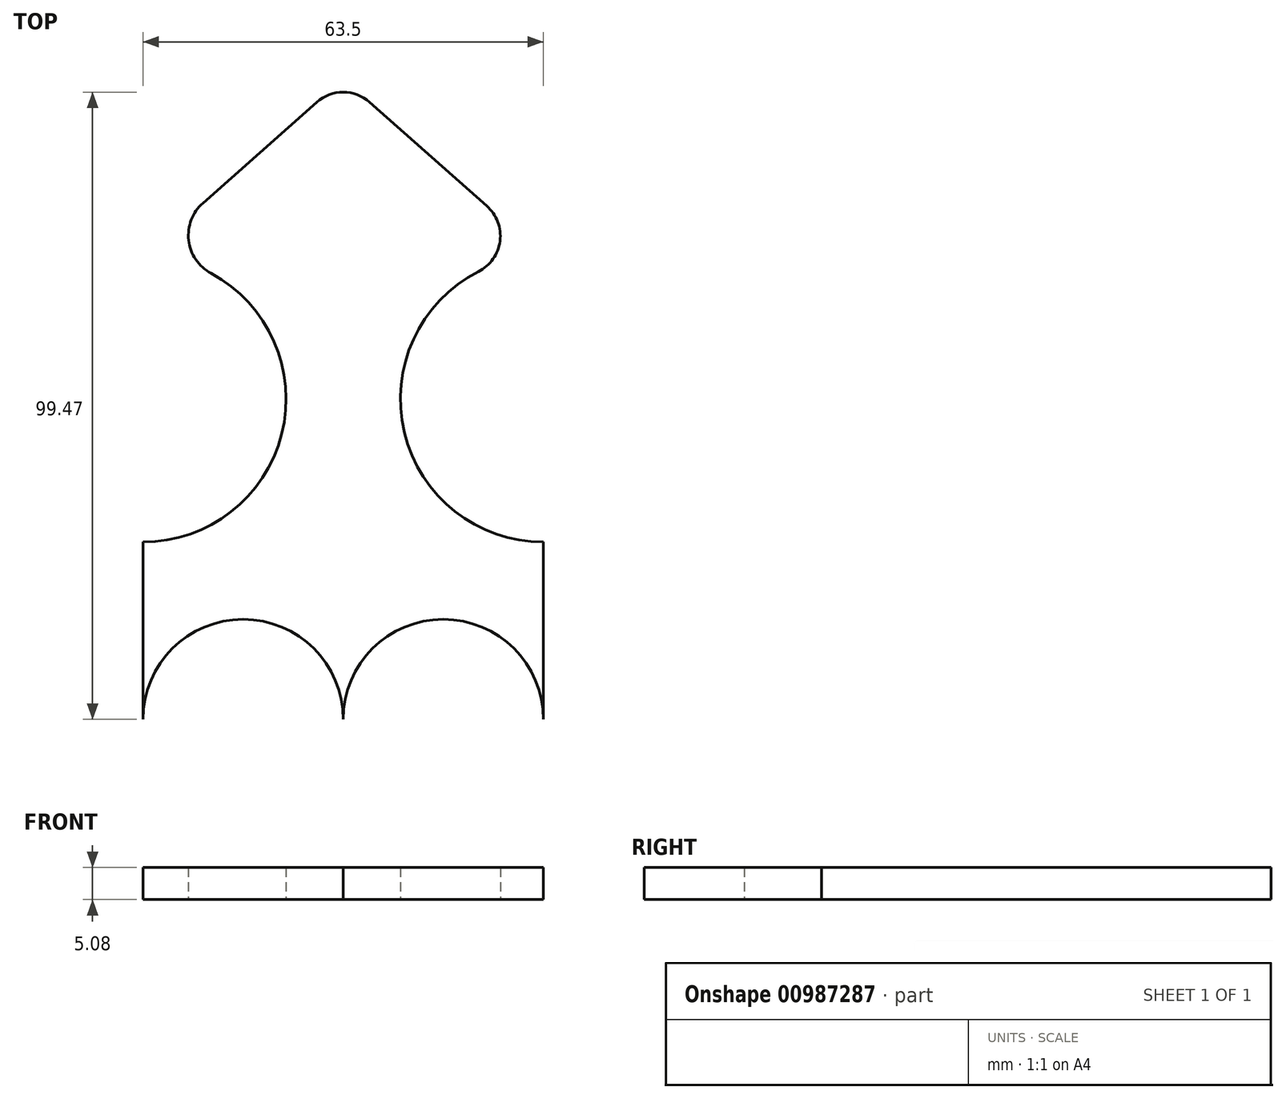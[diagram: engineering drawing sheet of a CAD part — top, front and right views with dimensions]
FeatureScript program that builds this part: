
annotation { "Feature Type Name" : "Feature", "Feature Type Description" : "" }
export const myFeature = defineFeature(function(context is Context, id is Id, definition is map)
    precondition{}
    {
        {
            var Q0;
            Q0=qCreatedBy(makeId("Top.planeOp"),FACE);
            var sketch = newSketch(context, id + "F0", { "sketchPlane" : qUnion([Q0])});
            skLineSegment(sketch, "E0", {"start": v(-31.75, 0) * mm, "end": v(-31.75, -101.6) * mm, "construction": true});
            skLineSegment(sketch, "E1", {"start": v(0, -50.8) * mm, "end": v(-63.5, -50.8) * mm, "construction": true});
            skArc(sketch, "E2", {"start": v(-63.5, -73.48) * mm, "mid": v(-41.5, -56.36) * mm, "end": v(-52.72, -30.84) * mm});
            skArc(sketch, "E3.1.0.0", {"start": v(-10.3, -30.59) * mm, "mid": v(-22.06, -56.1) * mm, "end": v(0, -73.48) * mm});
            skLineSegment(sketch, "E3.direction1", {"start": v(-63.5, -50.8) * mm, "end": v(0, -50.8) * mm, "construction": true});
            skLineSegment(sketch, "E4.trimOffspring", {"start": v(-63.5, -73.48) * mm, "end": v(-63.5, -101.6) * mm});
            skLineSegment(sketch, "E5.trimOffspring", {"start": v(0, -73.48) * mm, "end": v(0, -101.6) * mm});
            skArc(sketch, "E6", {"start": v(-31.75, -101.6) * mm, "mid": v(-47.62, -85.73) * mm, "end": v(-63.5, -101.6) * mm});
            skArc(sketch, "E7", {"start": v(0, -101.6) * mm, "mid": v(-15.88, -85.73) * mm, "end": v(-31.75, -101.6) * mm});
            skLineSegment(sketch, "E8", {"start": v(-8.97, -20.18) * mm, "end": v(-27.54, -3.73) * mm});
            skLineSegment(sketch, "E9", {"start": v(-35.96, -3.73) * mm, "end": v(-54, -19.7) * mm});
            skPoint(sketch, "E10.left.start.orphan", {"position": v(0, 0) * mm});
            skPoint(sketch, "E10.right.start.orphan", {"position": v(-63.5, 0) * mm});
            skPoint(sketch, "E11.visualSharp", {"position": v(-31.75, 0) * mm});
            skArc(sketch, "E11.filletArc", {"start": v(-27.54, -3.73) * mm, "mid": v(-31.75, -2.13) * mm, "end": v(-35.96, -3.73) * mm});
            skPoint(sketch, "E12.visualSharp", {"position": v(0, -28.12) * mm});
            skArc(sketch, "E12.filletArc", {"start": v(-10.3, -30.59) * mm, "mid": v(-6.88, -25.73) * mm, "end": v(-8.97, -20.18) * mm});
            skPoint(sketch, "E13.visualSharp", {"position": v(-63.5, -28.12) * mm});
            skArc(sketch, "E13.filletArc", {"start": v(-54, -19.7) * mm, "mid": v(-56.26, -25.6) * mm, "end": v(-52.72, -30.84) * mm});
            skSolve(sketch);
        }
        {
            var Q0;
            Q0=makeQuery(id+"F0.imprint","IMPRINT",FACE,{"disambiguationData":[TD([[makeQuery(id+"F0.imprint","IMPRINT",EDGE,{"derivedFrom":sQuery(id+"F0.wireOp",EDGE,"E2")}),-1.0]])]});
            extrude(context, id + "F1", {"entities" : qUnion([Q0]), "depth" : 5.08 * mm, "offsetDistance" : 25.4 * mm});
        }
    });
